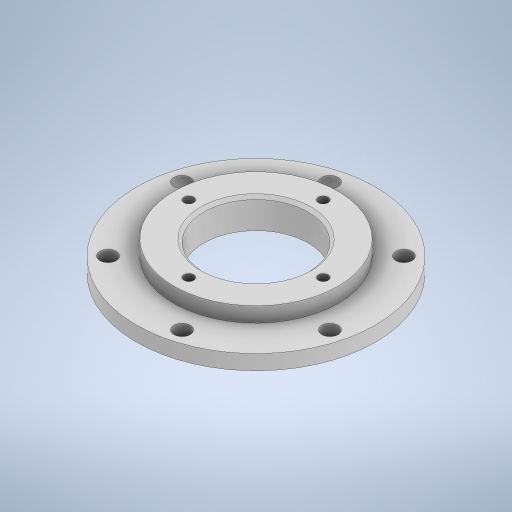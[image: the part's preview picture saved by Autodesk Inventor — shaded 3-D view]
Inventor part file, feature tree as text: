
AUTODESK INVENTOR PART (.ipt)
format: ipt  version: 2023.2 (Build 272271030, 271C)  size: 308,736 bytes
history: native  units: mm
features: sketch x3, hole x2, pattern_circular x2, projected_geometry x2, other x1, revolve x1, chamfer x1
ambient origin geometry x8: Origin, YZ Plane, XZ Plane, XY Plane, X Axis, Y Axis, Z Axis, Center Point
bodies: Body1 (feature_tree)
feature tree (12):
  other  "Твердое тело1"
  revolve  "Вращение1"
  hole  "Отверстие1"  [1 undecoded]
  pattern_circular  "Круговой массив1"  Count=11  [1 undecoded]
  hole  "Отверстие2"  [1 undecoded]
  pattern_circular  "Круговой массив2"  [2 undecoded]
  chamfer  "Фаска2"  Angle=90.0deg  [1 undecoded]
  sketch  "Эскиз1"
  sketch  "Эскиз2"
  projected_geometry  "Спроецированная петля1"
  sketch  "Эскиз3"
  projected_geometry  "Спроецированная петля2"
note: 6 required parameter values undecoded (feature->parameter linkage not recoverable at this tier; creation-order binding heuristic only, values carry confidence <= 0.55)
